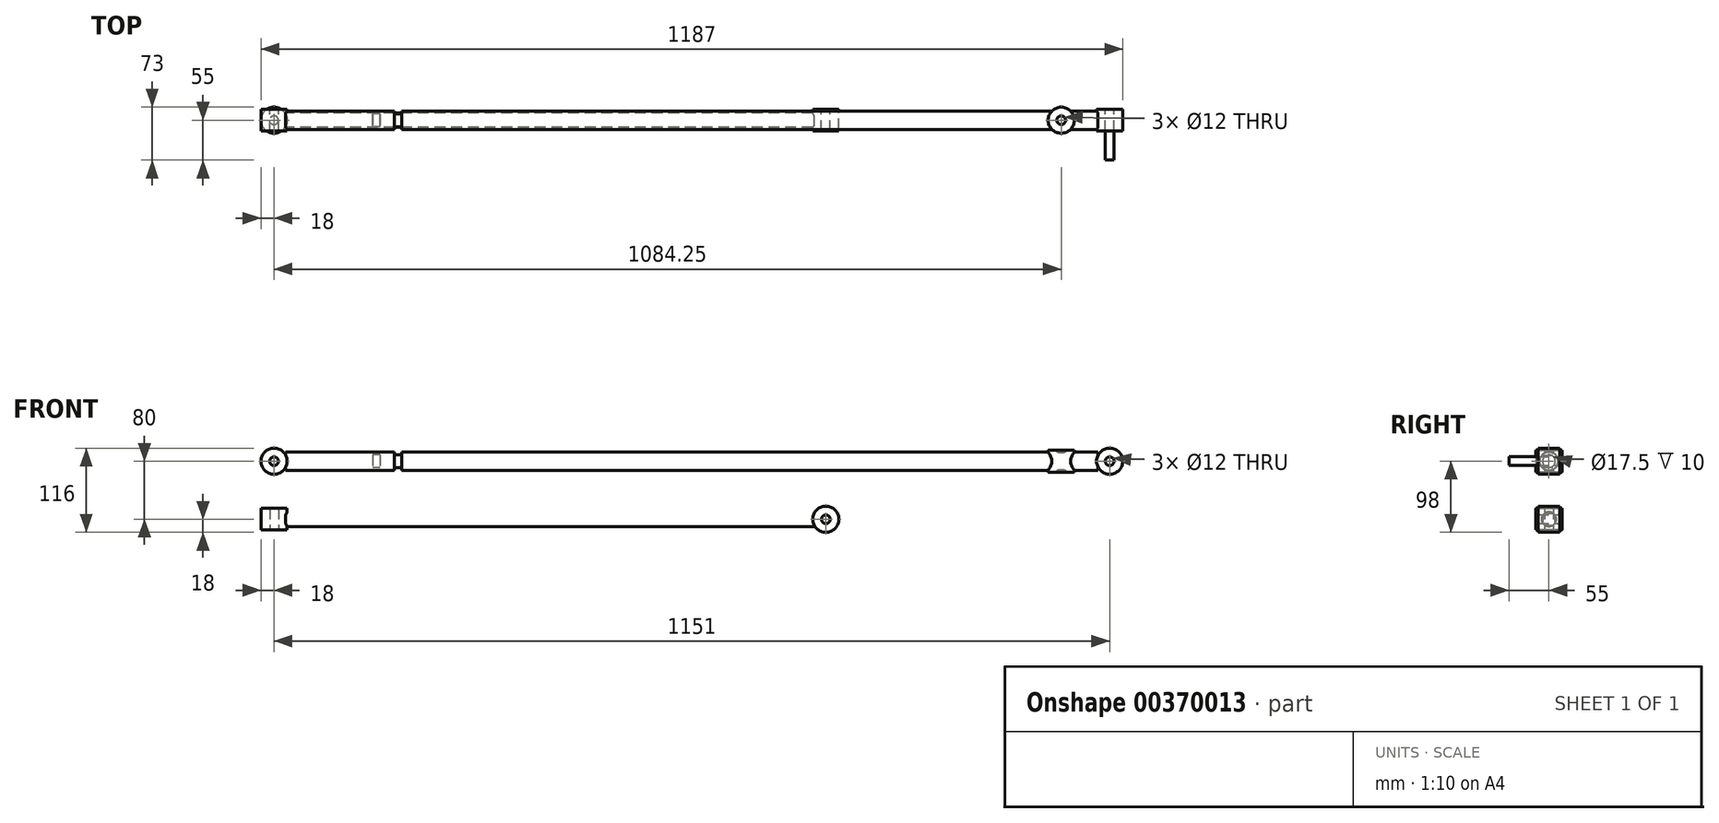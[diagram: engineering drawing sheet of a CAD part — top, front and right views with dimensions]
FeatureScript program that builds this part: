
annotation { "Feature Type Name" : "Feature", "Feature Type Description" : "" }
export const myFeature = defineFeature(function(context is Context, id is Id, definition is map)
    precondition{}
    {
        {
            var Q0;
            Q0=qCreatedBy(makeId("Front.planeOp"),FACE);
            var sketch = newSketch(context, id + "F0", { "sketchPlane" : qUnion([Q0])});
            skLineSegment(sketch, "E0", {"start": v(0, 0) * mm, "end": v(16, 0) * mm});
            skLineSegment(sketch, "E1", {"start": v(16, 0) * mm, "end": v(1135, 0) * mm});
            skLineSegment(sketch, "E2", {"start": v(1135, 0) * mm, "end": v(1135, 12.75) * mm});
            skLineSegment(sketch, "E3", {"start": v(1135, 12.75) * mm, "end": v(16, 12.75) * mm});
            skLineSegment(sketch, "E4", {"start": v(16, 12.75) * mm, "end": v(16, 0) * mm});
            skPoint(sketch, "E5", {"position": v(16, 12.75) * mm});
            skPoint(sketch, "E6", {"position": v(166, 12.75) * mm});
            skPoint(sketch, "E7", {"position": v(166, 0) * mm});
            skLineSegment(sketch, "E8", {"start": v(166, 12.75) * mm, "end": v(166, 8.75) * mm});
            skLineSegment(sketch, "E9", {"start": v(166, 8.75) * mm, "end": v(146, 8.75) * mm});
            skLineSegment(sketch, "E10", {"start": v(146, 8.75) * mm, "end": v(146, 0) * mm});
            skLineSegment(sketch, "E11", {"start": v(166, 0) * mm, "end": v(156, 0) * mm});
            skLineSegment(sketch, "E12", {"start": v(166, 8.75) * mm, "end": v(176, 8.75) * mm});
            skLineSegment(sketch, "E13", {"start": v(176, 8.75) * mm, "end": v(176, 12.75) * mm});
            skLineSegment(sketch, "E14", {"start": v(146, 8.75) * mm, "end": v(136, 8.75) * mm});
            skLineSegment(sketch, "E15", {"start": v(136, 8.75) * mm, "end": v(136, 0) * mm});
            skSolve(sketch);
        }
        {
            var Q0;
            {var subQ1=sQuery(id+"F0.wireOp",EDGE,"E4");Q0=makeQuery(id+"F0.imprint","IMPRINT",FACE,{"disambiguationData":[TD([[makeQuery(id+"F0.imprint","IMPRINT",EDGE,{"derivedFrom":subQ1}),1.0]])]});}
            var Q1;
            {var subQ1=sQuery(id+"F0.wireOp",EDGE,"E2");Q1=makeQuery(id+"F0.imprint","IMPRINT",FACE,{"disambiguationData":[TD([[makeQuery(id+"F0.imprint","IMPRINT",EDGE,{"derivedFrom":subQ1}),1.0]])]});}
            var Q2;
            Q2=sQuery(id+"F0.wireOp",EDGE,"E1");
            revolve(context, id + "F1", {"entities" : qUnion([Q0, Q1]), "axis" : qUnion([Q2]), "revolveType" : RevolveType.FULL});
        }
        {
            var Q0;
            Q0=qCreatedBy(makeId("Front.planeOp"),FACE);
            var sketch = newSketch(context, id + "F2", { "sketchPlane" : qUnion([Q0])});
            skCircle(sketch, "E16", {"center": v(0, 0) * mm, "radius": 18 * mm});
            skCircle(sketch, "E17", {"center": v(0, 0) * mm, "radius": 6 * mm});
            skPoint(sketch, "E18", {"position": v(1151, 0) * mm});
            skCircle(sketch, "E19", {"center": v(1151, 0) * mm, "radius": 18 * mm});
            skCircle(sketch, "E20", {"center": v(1151, 0) * mm, "radius": 6 * mm});
            skPoint(sketch, "E21", {"position": v(1084.25, 0) * mm});
            skCircle(sketch, "E22", {"center": v(1084.25, 0) * mm, "radius": 18 * mm, "construction": true});
            skCircle(sketch, "E23", {"center": v(1084.25, 0) * mm, "radius": 6 * mm, "construction": true});
            skSolve(sketch);
        }
        {
            var Q0;
            Q0 = qSketchRegion(id + "F2", true);
            extrude(context, id + "F3", {"entities" : qUnion([Q0]), "operationType" : NewBodyOperationType.ADD, "endBound" : BoundingType.SYMMETRIC, "depth" : 30 * mm});
        }
        {
            var Q0;
            Q0=makeQuery(id+"F3.opExtrude","CAP_FACE",FACE,{"disambiguationData":[OSD([sQuery(id+"F2.wireOp",EDGE,"E19"),sQuery(id+"F2.wireOp",EDGE,"E20")])],"isStart":false});
            var sketch = newSketch(context, id + "F4", { "sketchPlane" : qUnion([Q0])});
            skCircle(sketch, "E24.0", {"center": v(1151, 0) * mm, "radius": 6 * mm});
            skSolve(sketch);
        }
        {
            var Q0;
            Q0 = qSketchRegion(id + "F4", true);
            extrude(context, id + "F5", {"entities" : qUnion([Q0]), "depth" : 40 * mm});
        }
        {
            var Q0;
            Q0=qCreatedBy(makeId("Front.planeOp"),FACE);
            var sketch = newSketch(context, id + "F6", { "sketchPlane" : qUnion([Q0])});
            skPoint(sketch, "E25", {"position": v(0, -80) * mm});
            skPoint(sketch, "E26", {"position": v(16, -80) * mm});
            skLineSegment(sketch, "E27", {"start": v(16, -80) * mm, "end": v(744, -80) * mm});
            skLineSegment(sketch, "E28", {"start": v(16, -80) * mm, "end": v(16, -70) * mm});
            skLineSegment(sketch, "E29", {"start": v(16, -70) * mm, "end": v(744, -70) * mm});
            skLineSegment(sketch, "E30", {"start": v(744, -70) * mm, "end": v(744, -80) * mm});
            skSolve(sketch);
        }
        {
            var Q0;
            Q0 = qSketchRegion(id + "F6", true);
            var Q1;
            Q1=sQuery(id+"F6.wireOp",EDGE,"E27");
            revolve(context, id + "F7", {"entities" : qUnion([Q0]), "axis" : qUnion([Q1]), "revolveType" : RevolveType.FULL});
        }
        {
            var Q0;
            Q0=qCreatedBy(makeId("Front.planeOp"),FACE);
            var sketch = newSketch(context, id + "F8", { "sketchPlane" : qUnion([Q0])});
            skPoint(sketch, "E31", {"position": v(0, -80) * mm});
            skCircle(sketch, "E32", {"center": v(0, -80) * mm, "radius": 18 * mm, "construction": true});
            skCircle(sketch, "E33", {"center": v(0, -80) * mm, "radius": 6 * mm, "construction": true});
            skPoint(sketch, "E34", {"position": v(760, -80) * mm});
            skCircle(sketch, "E35", {"center": v(760, -80) * mm, "radius": 18 * mm});
            skCircle(sketch, "E36", {"center": v(760, -80) * mm, "radius": 6 * mm});
            skSolve(sketch);
        }
        {
            var Q0;
            Q0 = qSketchRegion(id + "F8", true);
            extrude(context, id + "F9", {"entities" : qUnion([Q0]), "operationType" : NewBodyOperationType.ADD, "endBound" : BoundingType.SYMMETRIC, "depth" : 30 * mm});
        }
        {
            var Q0;
            Q0=qCreatedBy(makeId("Top.planeOp"),FACE);
            cPlane(context, id + "F10", {"entities" : qUnion([Q0]), "cplaneType" : CPlaneType.OFFSET, "offset" : 80 * mm, "oppositeDirection" : true, "width" : 150 * mm, "height" : 150 * mm});
        }
        {
            var Q0;
            Q0=qCreatedBy(id+"F10.planeOp",FACE);
            var sketch = newSketch(context, id + "F11", { "sketchPlane" : qUnion([Q0])});
            skCircle(sketch, "E37", {"center": v(0, 0) * mm, "radius": 18 * mm});
            skCircle(sketch, "E38", {"center": v(0, 0) * mm, "radius": 6 * mm});
            skSolve(sketch);
        }
        {
            var Q0;
            Q0 = qSketchRegion(id + "F11", true);
            extrude(context, id + "F12", {"entities" : qUnion([Q0]), "operationType" : NewBodyOperationType.ADD, "endBound" : BoundingType.SYMMETRIC, "depth" : 30 * mm});
        }
        {
            var Q0;
            Q0=qCreatedBy(makeId("Top.planeOp"),FACE);
            var sketch = newSketch(context, id + "F13", { "sketchPlane" : qUnion([Q0])});
            skLineSegment(sketch, "E39.0", {"start": v(1157, -55) * mm, "end": v(1145, -55) * mm});
            skPoint(sketch, "E40", {"position": v(1084.25, 0) * mm});
            skPoint(sketch, "E41", {"position": v(1151, -55) * mm});
            skCircle(sketch, "E42", {"center": v(1084.25, 0) * mm, "radius": 18 * mm});
            skCircle(sketch, "E43", {"center": v(1084.25, 0) * mm, "radius": 6 * mm});
            skSolve(sketch);
        }
        {
            var Q0;
            Q0 = qSketchRegion(id + "F13", true);
            extrude(context, id + "F14", {"entities" : qUnion([Q0]), "operationType" : NewBodyOperationType.ADD, "endBound" : BoundingType.SYMMETRIC, "depth" : 30 * mm});
        }
    });
